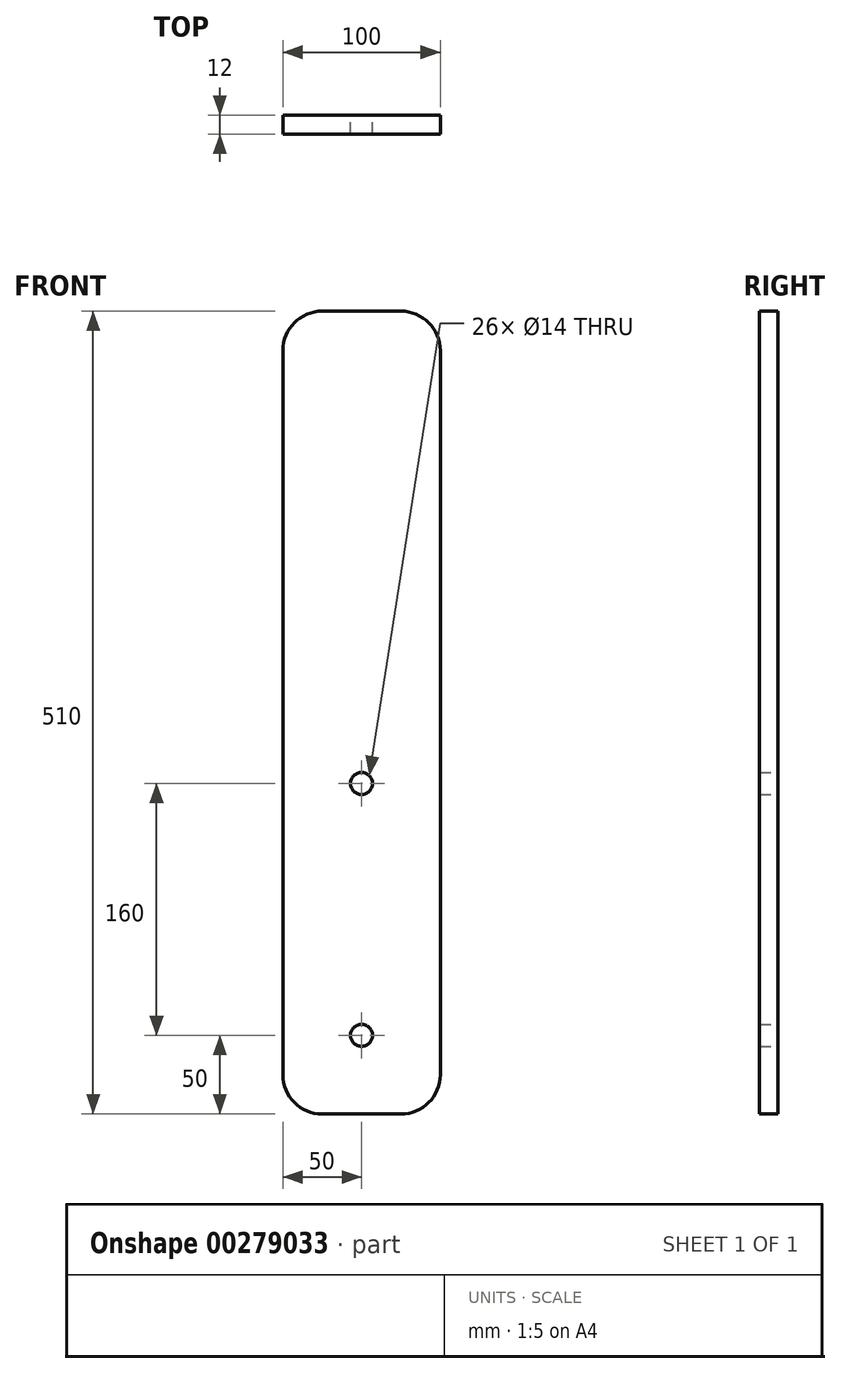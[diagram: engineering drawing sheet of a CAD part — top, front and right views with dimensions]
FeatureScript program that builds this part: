
annotation { "Feature Type Name" : "Feature", "Feature Type Description" : "" }
export const myFeature = defineFeature(function(context is Context, id is Id, definition is map)
    precondition{}
    {
        {
            var Q0;
            Q0=qCreatedBy(makeId("Front.planeOp"),FACE);
            var sketch = newSketch(context, id + "F0", { "sketchPlane" : qUnion([Q0])});
            skLineSegment(sketch, "E0.bottom", {"start": v(25, 0) * mm, "end": v(75, 0) * mm});
            skLineSegment(sketch, "E0.top", {"start": v(25, 510) * mm, "end": v(75, 510) * mm});
            skLineSegment(sketch, "E0.left", {"start": v(0, 25) * mm, "end": v(0, 485) * mm});
            skLineSegment(sketch, "E0.right", {"start": v(100, 25) * mm, "end": v(100, 485) * mm});
            skCircle(sketch, "E1", {"center": v(50, 210) * mm, "radius": 7 * mm});
            skCircle(sketch, "E2", {"center": v(50, 50) * mm, "radius": 7 * mm});
            skPoint(sketch, "E3.visualSharp", {"position": v(0, 510) * mm});
            skArc(sketch, "E3.filletArc", {"start": v(25, 510) * mm, "mid": v(7.32, 502.68) * mm, "end": v(0, 485) * mm});
            skPoint(sketch, "E4.visualSharp", {"position": v(100, 510) * mm});
            skArc(sketch, "E4.filletArc", {"start": v(100, 485) * mm, "mid": v(92.68, 502.68) * mm, "end": v(75, 510) * mm});
            skPoint(sketch, "E5.visualSharp", {"position": v(100, 0) * mm});
            skArc(sketch, "E5.filletArc", {"start": v(75, 0) * mm, "mid": v(92.68, 7.32) * mm, "end": v(100, 25) * mm});
            skPoint(sketch, "E6.visualSharp", {"position": v(0, 0) * mm});
            skArc(sketch, "E6.filletArc", {"start": v(0, 25) * mm, "mid": v(7.32, 7.32) * mm, "end": v(25, 0) * mm});
            skSolve(sketch);
        }
        {
            var Q0;
            Q0=makeQuery(id+"F0.imprint","IMPRINT",FACE,{"disambiguationData":[TD([[makeQuery(id+"F0.imprint","IMPRINT",EDGE,{"derivedFrom":sQuery(id+"F0.wireOp",EDGE,"E0.bottom")}),1.0]])]});
            extrude(context, id + "F1", {"entities" : qUnion([Q0]), "depth" : 12 * mm});
        }
    });
